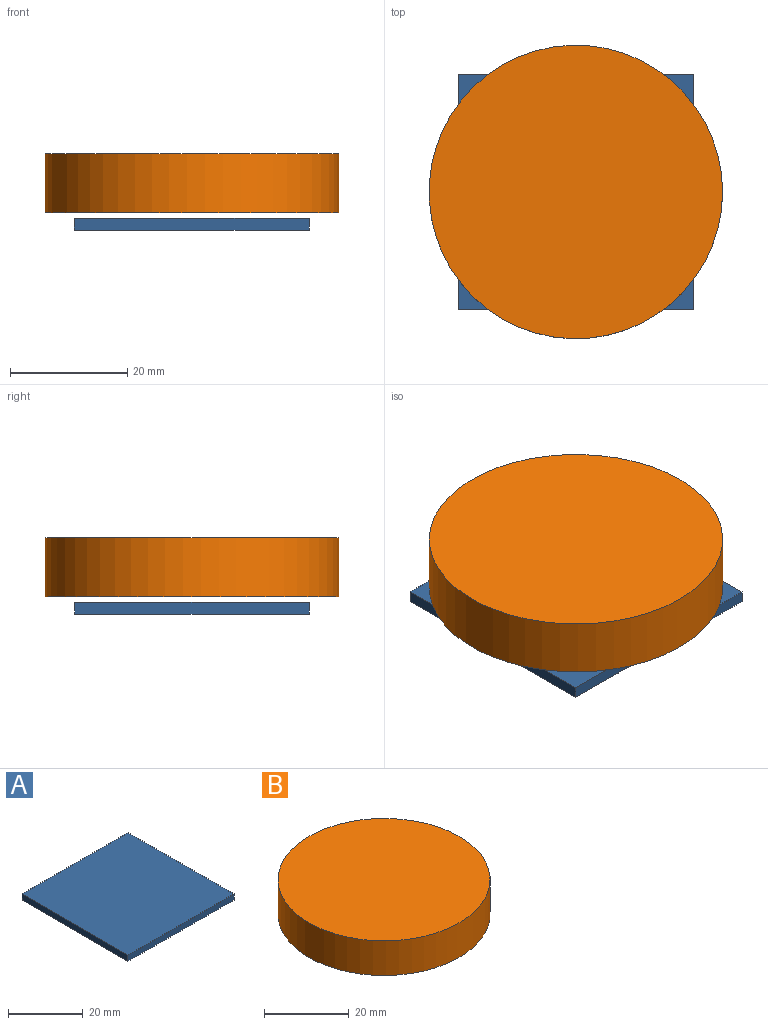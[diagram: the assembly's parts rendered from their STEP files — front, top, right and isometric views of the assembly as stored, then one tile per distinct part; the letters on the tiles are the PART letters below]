
ASSEMBLY  parts=2 mates=1
PART A: 6 faces, bbox 40x40x2 mm
  f0: plane 40x2mm, normal (0,-1,0), area 80mm2, adj f1,f3,f4,f5
  f1: plane 40x2mm, normal (1,0,0), area 80mm2, adj f0,f2,f4,f5
  f2: plane 40x2mm, normal (0,1,0), area 80mm2, adj f1,f3,f4,f5
  f3: plane 40x2mm, normal (-1,0,0), area 80mm2, adj f0,f2,f4,f5
  f4: plane 40x40mm, normal (0,0,-1), area 1600mm2, adj f0,f1,f2,f3
  f5: plane 40x40mm, normal (0,0,1), area 1600mm2, adj f0,f1,f2,f3
PART B: 3 faces, bbox 50x50x10 mm
  f0: cylinder r=25mm len=50mm, axis (0,0,-1), area 1570.8mm2, adj f1,f2
  f1: plane 50x50mm, normal (0,0,1), area 1963.5mm2, adj f0
  f2: plane 50x50mm, normal (0,0,-1), area 1963.5mm2, adj f0
PLACE A t=(0,0,3)mm
PLACE B t=(0,0,3)mm
MATE slider B.f0 <-> A.f5  axis (0,0,1) through (0,0,13)mm
